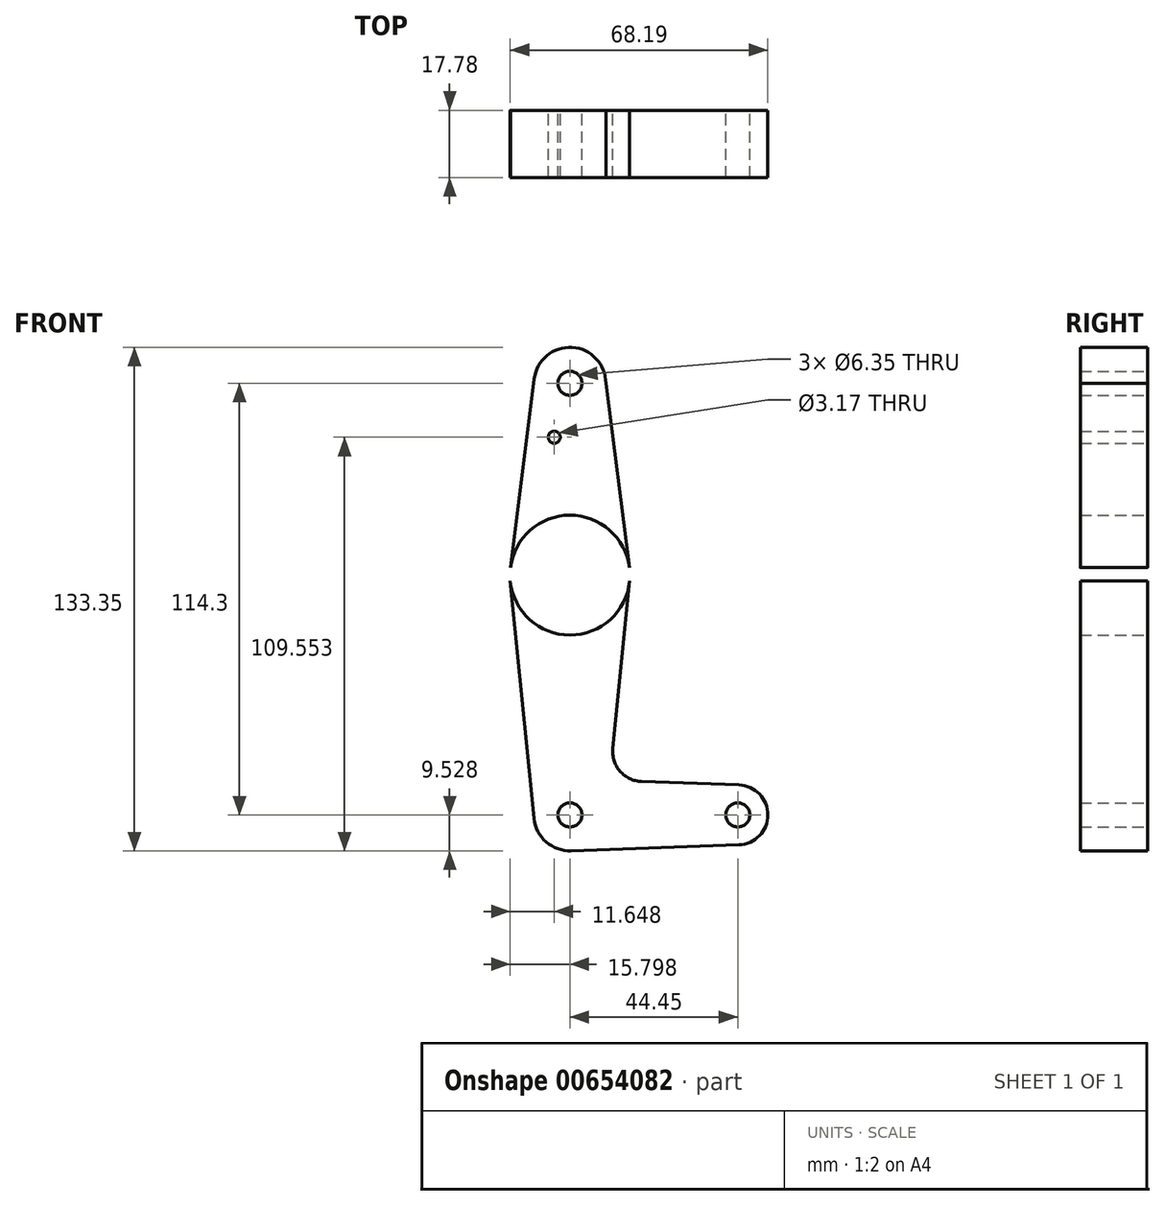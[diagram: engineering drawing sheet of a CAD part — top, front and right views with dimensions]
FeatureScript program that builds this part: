
annotation { "Feature Type Name" : "Feature", "Feature Type Description" : "" }
export const myFeature = defineFeature(function(context is Context, id is Id, definition is map)
    precondition{}
    {
        {
            var Q0;
            Q0=qCreatedBy(makeId("Front.planeOp"),FACE);
            var sketch = newSketch(context, id + "F0", { "sketchPlane" : qUnion([Q0])});
            skLineSegment(sketch, "E0", {"start": v(-36.71, 69.09) * mm, "end": v(-36.71, -45.21) * mm});
            skLineSegment(sketch, "E1", {"start": v(-36.71, -45.21) * mm, "end": v(7.74, -45.21) * mm});
            skCircle(sketch, "E2", {"center": v(-36.71, 18.29) * mm, "radius": 15.88 * mm});
            skCircle(sketch, "E3", {"center": v(-36.71, -45.21) * mm, "radius": 9.53 * mm});
            skCircle(sketch, "E4", {"center": v(7.74, -45.21) * mm, "radius": 7.94 * mm});
            skCircle(sketch, "E5", {"center": v(-36.71, 69.09) * mm, "radius": 9.53 * mm});
            skLineSegment(sketch, "E6", {"start": v(-52.5, 16.7) * mm, "end": v(-46.19, -46.16) * mm});
            skLineSegment(sketch, "E7", {"start": v(-27.19, 69.09) * mm, "end": v(-20.96, 20.3) * mm});
            skLineSegment(sketch, "E8", {"start": v(-17.74, -36.36) * mm, "end": v(8.02, -37.28) * mm});
            skLineSegment(sketch, "E9", {"start": v(-36.37, -54.73) * mm, "end": v(8.02, -53.14) * mm});
            skLineSegment(sketch, "E10", {"start": v(-46.16, 70.28) * mm, "end": v(-52.46, 20.27) * mm});
            skLineSegment(sketch, "E11", {"start": v(-20.92, 16.7) * mm, "end": v(-25.37, -27.62) * mm});
            skCircle(sketch, "E12", {"center": v(-36.71, 69.09) * mm, "radius": 3.18 * mm});
            skCircle(sketch, "E13", {"center": v(-36.71, 18.29) * mm, "radius": 3.18 * mm});
            skCircle(sketch, "E14", {"center": v(-36.71, -45.21) * mm, "radius": 3.18 * mm});
            skCircle(sketch, "E15", {"center": v(7.74, -45.21) * mm, "radius": 3.18 * mm});
            skArc(sketch, "E16.filletArc", {"start": v(-25.37, -27.62) * mm, "mid": v(-23.45, -33.64) * mm, "end": v(-17.74, -36.36) * mm});
            skCircle(sketch, "E17", {"center": v(-40.86, 54.81) * mm, "radius": 1.59 * mm});
            skSolve(sketch);
        }
        {
            var Q0;
            Q0=makeQuery(id+"F0.imprint","IMPRINT",FACE,{"disambiguationData":[TD([[makeQuery(id+"F0.imprint","IMPRINT",EDGE,{"derivedFrom":sQuery(id+"F0.wireOp",EDGE,"E12")}),-1.0]])]});
            var Q1;
            {var subQ0=sQuery(id+"F0.wireOp",EDGE,"E10");Q1=makeQuery(id+"F0.imprint","IMPRINT",FACE,{"disambiguationData":[TD([[makeQuery(id+"F0.imprint","IMPRINT",EDGE,{"derivedFrom":subQ0}),1.0]])]});}
            var Q2;
            {var subQ5=sQuery(id+"F0.wireOp",EDGE,"E7");Q2=makeQuery(id+"F0.imprint","IMPRINT",FACE,{"disambiguationData":[TD([[makeQuery(id+"F0.imprint","IMPRINT",EDGE,{"derivedFrom":subQ5}),-1.0]])]});}
            var Q3;
            {var subQ0=sQuery(id+"F0.wireOp",EDGE,"E2");var subQ3=sQuery(id+"F0.wireOp",EDGE,"E0");var subQ4=makeQuery(id+"F0.imprint","INTERSECT",VERTEX,{"disambiguationData":[OD(0.0)],"derivedFrom":[subQ3,subQ0]});Q3=makeQuery(id+"F0.imprint","IMPRINT",FACE,{"disambiguationData":[TD([[makeQuery(id+"F0.imprint","IMPRINT",EDGE,{"disambiguationData":[TD([[subQ4,-1.0]])],"derivedFrom":subQ3}),-1.0]])]});}
            var Q4;
            {var subQ0=sQuery(id+"F0.wireOp",EDGE,"E2");var subQ2=sQuery(id+"F0.wireOp",EDGE,"E0");var subQ7=makeQuery(id+"F0.imprint","INTERSECT",VERTEX,{"disambiguationData":[OD(0.0)],"derivedFrom":[subQ2,subQ0]});Q4=makeQuery(id+"F0.imprint","IMPRINT",FACE,{"disambiguationData":[TD([[makeQuery(id+"F0.imprint","IMPRINT",EDGE,{"disambiguationData":[TD([[subQ7,-1.0]])],"derivedFrom":subQ2}),1.0]])]});}
            var Q5;
            {var subQ5=sQuery(id+"F0.wireOp",EDGE,"E6");Q5=makeQuery(id+"F0.imprint","IMPRINT",FACE,{"disambiguationData":[TD([[makeQuery(id+"F0.imprint","IMPRINT",EDGE,{"derivedFrom":subQ5}),1.0]])]});}
            var Q6;
            {var subQ10=sQuery(id+"F0.wireOp",EDGE,"E8");Q6=makeQuery(id+"F0.imprint","IMPRINT",FACE,{"disambiguationData":[TD([[makeQuery(id+"F0.imprint","IMPRINT",EDGE,{"derivedFrom":subQ10}),-1.0]])]});}
            var Q7;
            {var subQ0=sQuery(id+"F0.wireOp",EDGE,"E3");var subQ2=sQuery(id+"F0.wireOp",EDGE,"E0");var subQ3=makeQuery(id+"F0.imprint","INTERSECT",VERTEX,{"derivedFrom":[subQ2,subQ0]});Q7=makeQuery(id+"F0.imprint","IMPRINT",FACE,{"disambiguationData":[TD([[makeQuery(id+"F0.imprint","IMPRINT",EDGE,{"disambiguationData":[TD([[subQ3,-1.0]])],"derivedFrom":subQ2}),-1.0]])]});}
            var Q8;
            {var subQ0=sQuery(id+"F0.wireOp",EDGE,"E3");var subQ1=sQuery(id+"F0.wireOp",EDGE,"E0");var subQ2=makeQuery(id+"F0.imprint","INTERSECT",VERTEX,{"derivedFrom":[subQ1,subQ0]});Q8=makeQuery(id+"F0.imprint","IMPRINT",FACE,{"disambiguationData":[TD([[makeQuery(id+"F0.imprint","IMPRINT",EDGE,{"disambiguationData":[TD([[subQ2,-1.0]])],"derivedFrom":subQ1}),1.0]])]});}
            var Q9;
            Q9=makeQuery(id+"F0.imprint","IMPRINT",FACE,{"disambiguationData":[TD([[makeQuery(id+"F0.imprint","IMPRINT",EDGE,{"derivedFrom":sQuery(id+"F0.wireOp",EDGE,"E15")}),-1.0]])]});
            var Q10;
            {var subQ5=sQuery(id+"F0.wireOp",EDGE,"E9");Q10=makeQuery(id+"F0.imprint","IMPRINT",FACE,{"disambiguationData":[TD([[makeQuery(id+"F0.imprint","IMPRINT",EDGE,{"derivedFrom":subQ5}),1.0]])]});}
            extrude(context, id + "F1", {"entities" : qUnion([Q0, Q1, Q2, Q3, Q4, Q5, Q6, Q7, Q8, Q9, Q10]), "depth" : 17.78 * mm, "offsetDistance" : 25.4 * mm});
        }
    });
